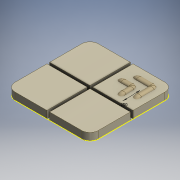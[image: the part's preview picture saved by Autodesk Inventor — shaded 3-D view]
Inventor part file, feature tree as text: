
AUTODESK INVENTOR PART (.ipt)
format: ipt  version: 2018 (Build 220112000, 112)  size: 408,576 bytes
history: native  units: in
note: dims shown in document units (in); Inventor stores cm internally (conversion verified against a paired STEP export)
features: other x14, extrude x2, plane x2, sweep x2, sketch x2, pattern_circular x1, split x1, mirror x1
ambient origin geometry x8: Origin, YZ Plane, XZ Plane, XY Plane, X Axis, Y Axis, Z Axis, Center Point
bodies: Solid29 (feature_tree), Solid30 (feature_tree), Solid31 (feature_tree), Solid32 (feature_tree), Solid33 (feature_tree)
feature tree (25):
  other  "Remote Buttons.ipt"
  other  "Work Axis1"
  extrude  "Extrusion7"  Depth=0.3937in TaperAngle=360.0deg
  pattern_circular  "Circular Pattern1"  [2 undecoded]
  other  "Bottom Plane"
  other  "Top Plane"
  other  "North Ridge Mirror Plane"
  other  "North Ridge Layout Sketch"
  other  "North Ridge Plane 1"
  plane  "Work Plane15"
  sweep  "Sweep1"
  plane  "Work Plane16"
  sweep  "Sweep2"
  other  "Bend Part1"
  other  "Bend Part2"
  split  "Split1"
  mirror  "Mirror2"
  extrude  "Extrusion8"  Depth=0.04in
  other  "Pattern of Solid29:7"
  other  "Pattern of Solid29:8"
  other  "Pattern of Solid29:9"
  sketch  "Sketch39"  dims[d0=0.3937in d3=1.5748in d4=360.0deg]
  sketch  "Sketch40"  dims[d20=0.1562in d200=0.3047in d201=0.2344in d202=0.1562in d203=0.04in d204=0.022in d205=0.0in d206=0.0in d207=0.1562in d208=0.0312in d209=0.2344in d210=0.0in d211=0.04in d212=0.022in d213=0.0in d214=0.0in d215=0.1in d216=90.0deg d217=0.0312in d218=0.1in d219=0.6184in d274=0.109in d275=0.0in d276=0.075in d277=0.0in d278=0.25in]
  other  "Button Base Sketch"
  other  "Peg Sketch"
note: 2 required parameter values undecoded (feature->parameter linkage not recoverable at this tier; creation-order binding heuristic only, values carry confidence <= 0.55)
